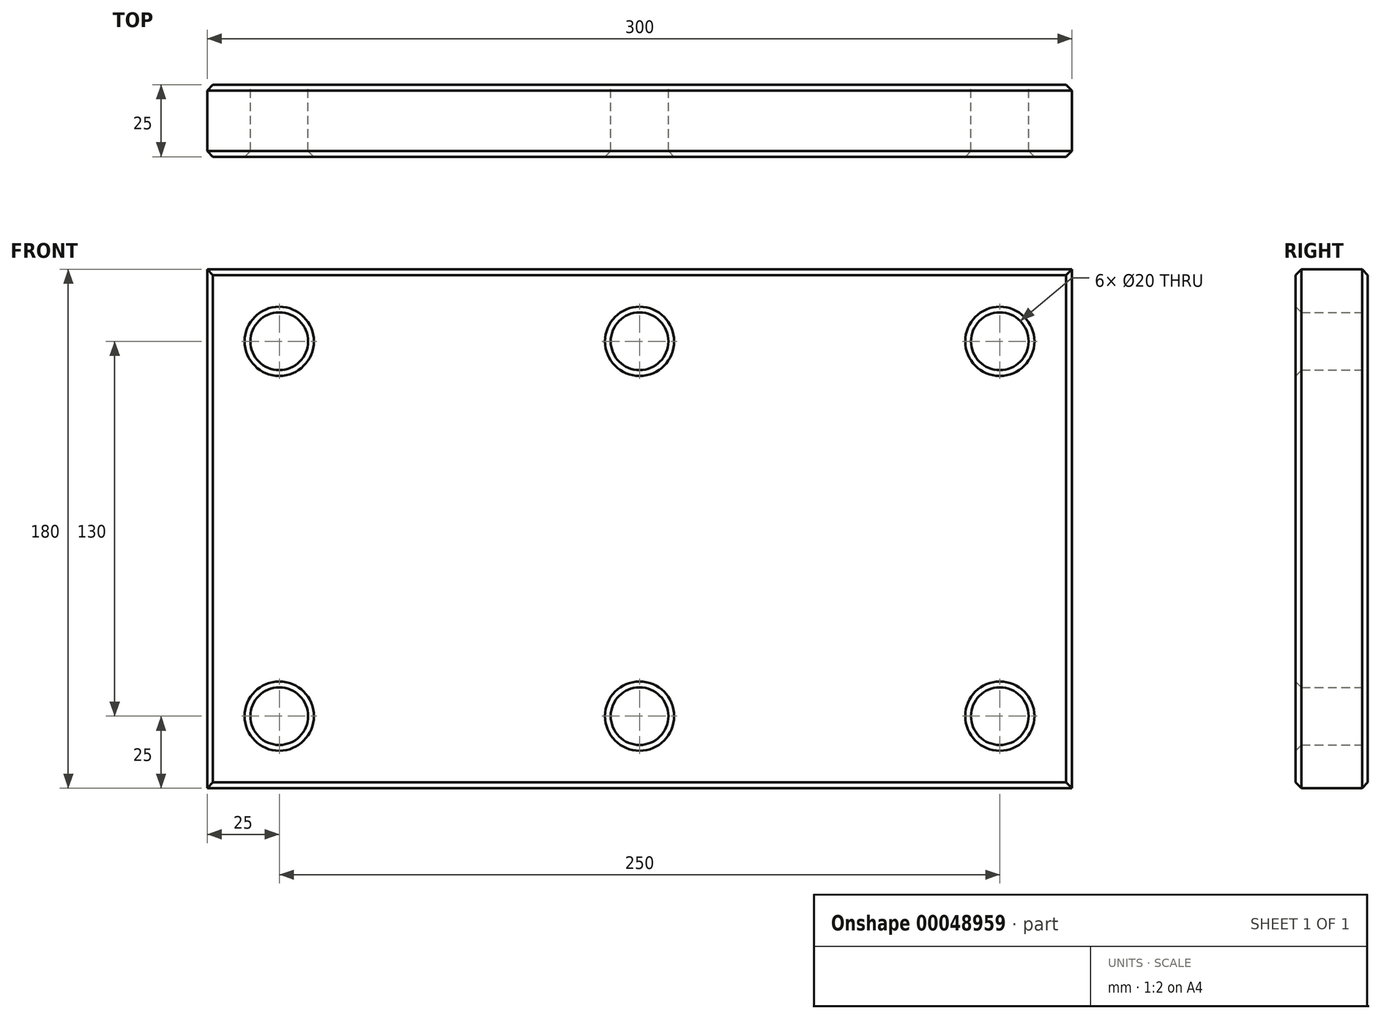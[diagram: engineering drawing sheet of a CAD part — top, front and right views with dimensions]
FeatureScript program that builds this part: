
annotation { "Feature Type Name" : "Feature", "Feature Type Description" : "" }
export const myFeature = defineFeature(function(context is Context, id is Id, definition is map)
    precondition{}
    {
        {
            var Q0;
            Q0=qCreatedBy(makeId("Front.planeOp"),FACE);
            var sketch = newSketch(context, id + "F0", { "sketchPlane" : qUnion([Q0])});
            skLineSegment(sketch, "E0.bottom", {"start": v(0, 180) * mm, "end": v(300, 180) * mm});
            skLineSegment(sketch, "E0.top", {"start": v(0, 0) * mm, "end": v(300, 0) * mm});
            skLineSegment(sketch, "E0.left", {"start": v(0, 180) * mm, "end": v(0, 0) * mm});
            skLineSegment(sketch, "E0.right", {"start": v(300, 180) * mm, "end": v(300, 0) * mm});
            skLineSegment(sketch, "E1.bottom", {"start": v(25, 155) * mm, "end": v(275, 155) * mm, "construction": true});
            skLineSegment(sketch, "E1.top", {"start": v(25, 25) * mm, "end": v(275, 25) * mm, "construction": true});
            skLineSegment(sketch, "E1.left", {"start": v(25, 155) * mm, "end": v(25, 25) * mm, "construction": true});
            skLineSegment(sketch, "E1.right", {"start": v(275, 155) * mm, "end": v(275, 25) * mm, "construction": true});
            skLineSegment(sketch, "E2", {"start": v(150, 155) * mm, "end": v(150, 25) * mm, "construction": true});
            skCircle(sketch, "E3", {"center": v(25, 155) * mm, "radius": 10 * mm});
            skCircle(sketch, "E4", {"center": v(150, 155) * mm, "radius": 10 * mm});
            skCircle(sketch, "E5", {"center": v(275, 155) * mm, "radius": 10 * mm});
            skCircle(sketch, "E6", {"center": v(25, 25) * mm, "radius": 10 * mm});
            skCircle(sketch, "E7", {"center": v(150, 25) * mm, "radius": 10 * mm});
            skCircle(sketch, "E8", {"center": v(275, 25) * mm, "radius": 10 * mm});
            skSolve(sketch);
        }
        {
            var Q0;
            Q0=makeQuery(id+"F0.imprint","IMPRINT",FACE,{"disambiguationData":[TD([[makeQuery(id+"F0.imprint","IMPRINT",EDGE,{"derivedFrom":sQuery(id+"F0.wireOp",EDGE,"E0.bottom")}),-1.0]])]});
            extrude(context, id + "F1", {"entities" : qUnion([Q0]), "depth" : 25 * mm});
        }
        {
            var Q0;
            Q0=makeQuery(id+"F1.opExtrude","CAP_EDGE",EDGE,{"disambiguationData":[OSD([sQuery(id+"F0.wireOp",EDGE,"E3")])],"isStart":false});
            var Q1;
            Q1=makeQuery(id+"F1.opExtrude","CAP_EDGE",EDGE,{"disambiguationData":[OSD([sQuery(id+"F0.wireOp",EDGE,"E6")])],"isStart":false});
            var Q2;
            Q2=makeQuery(id+"F1.opExtrude","CAP_EDGE",EDGE,{"disambiguationData":[OSD([sQuery(id+"F0.wireOp",EDGE,"E7")])],"isStart":false});
            var Q3;
            Q3=makeQuery(id+"F1.opExtrude","CAP_EDGE",EDGE,{"disambiguationData":[OSD([sQuery(id+"F0.wireOp",EDGE,"E4")])],"isStart":false});
            var Q4;
            Q4=makeQuery(id+"F1.opExtrude","CAP_EDGE",EDGE,{"disambiguationData":[OSD([sQuery(id+"F0.wireOp",EDGE,"E5")])],"isStart":false});
            var Q5;
            Q5=makeQuery(id+"F1.opExtrude","CAP_EDGE",EDGE,{"disambiguationData":[OSD([sQuery(id+"F0.wireOp",EDGE,"E8")])],"isStart":false});
            chamfer(context, id + "F2", {"entities" : qUnion([Q0, Q1, Q2, Q3, Q4, Q5]), "chamferType" : ChamferType.OFFSET_ANGLE, "width" : 2 * mm, "oppositeDirection" : false, "angle" : 45 * degree, "tangentPropagation" : true});
        }
        {
            var Q0;
            Q0=makeQuery(id+"F1.opExtrude","CAP_EDGE",EDGE,{"disambiguationData":[OSD([sQuery(id+"F0.wireOp",EDGE,"E0.right")])],"isStart":false});
            var Q1;
            Q1=makeQuery(id+"F1.opExtrude","CAP_EDGE",EDGE,{"disambiguationData":[OSD([sQuery(id+"F0.wireOp",EDGE,"E0.top")])],"isStart":false});
            var Q2;
            Q2=makeQuery(id+"F1.opExtrude","CAP_EDGE",EDGE,{"disambiguationData":[OSD([sQuery(id+"F0.wireOp",EDGE,"E0.left")])],"isStart":false});
            var Q3;
            Q3=makeQuery(id+"F1.opExtrude","CAP_EDGE",EDGE,{"disambiguationData":[OSD([sQuery(id+"F0.wireOp",EDGE,"E0.bottom")])],"isStart":false});
            var Q4;
            Q4=makeQuery(id+"F1.opExtrude","CAP_EDGE",EDGE,{"disambiguationData":[OSD([sQuery(id+"F0.wireOp",EDGE,"E0.top")])],"isStart":true});
            var Q5;
            Q5=makeQuery(id+"F1.opExtrude","CAP_EDGE",EDGE,{"disambiguationData":[OSD([sQuery(id+"F0.wireOp",EDGE,"E0.left")])],"isStart":true});
            var Q6;
            Q6=makeQuery(id+"F1.opExtrude","CAP_EDGE",EDGE,{"disambiguationData":[OSD([sQuery(id+"F0.wireOp",EDGE,"E0.right")])],"isStart":true});
            var Q7;
            Q7=makeQuery(id+"F1.opExtrude","CAP_EDGE",EDGE,{"disambiguationData":[OSD([sQuery(id+"F0.wireOp",EDGE,"E0.bottom")])],"isStart":true});
            chamfer(context, id + "F3", {"entities" : qUnion([Q0, Q1, Q2, Q3, Q4, Q5, Q6, Q7]), "chamferType" : ChamferType.OFFSET_ANGLE, "width" : 2 * mm, "oppositeDirection" : false, "angle" : 45 * degree, "tangentPropagation" : true});
        }
    });
